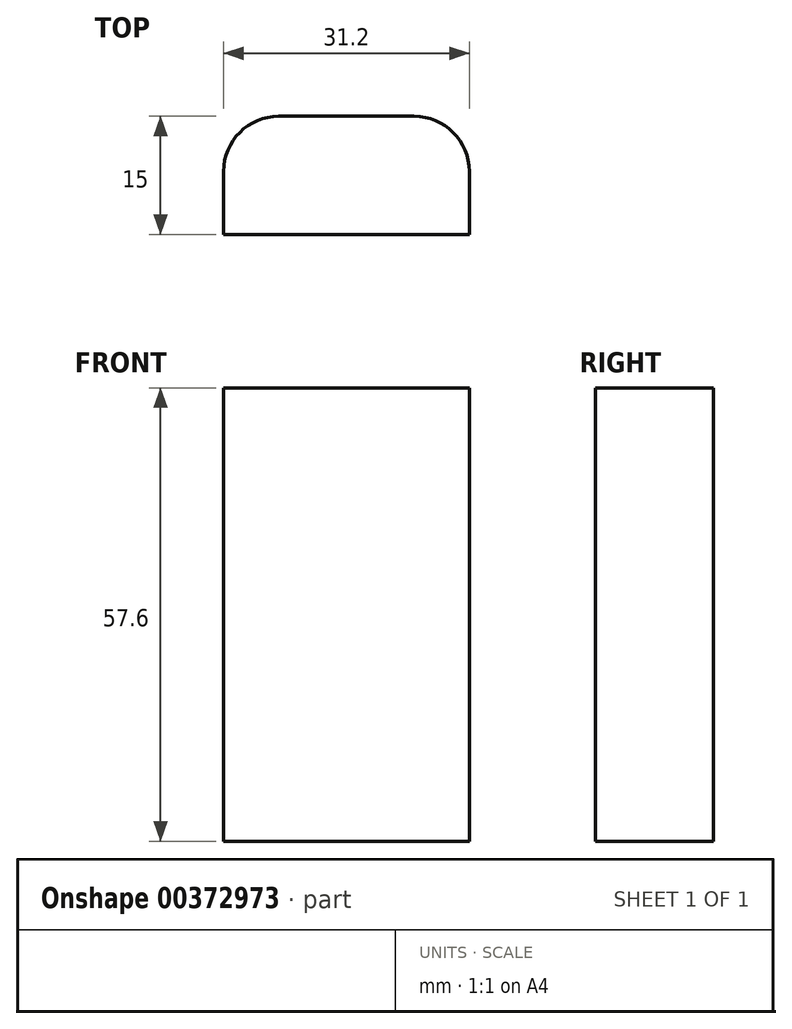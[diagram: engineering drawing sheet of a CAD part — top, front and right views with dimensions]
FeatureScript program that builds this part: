
annotation { "Feature Type Name" : "Feature", "Feature Type Description" : "" }
export const myFeature = defineFeature(function(context is Context, id is Id, definition is map)
    precondition{}
    {
        {
            var Q0;
            Q0=qCreatedBy(makeId("Top.planeOp"),FACE);
            var sketch = newSketch(context, id + "F0", { "sketchPlane" : qUnion([Q0])});
            skLineSegment(sketch, "E0.bottom", {"start": v(7, 15) * mm, "end": v(24.2, 15) * mm});
            skLineSegment(sketch, "E0.top", {"start": v(0, 0) * mm, "end": v(31.2, 0) * mm});
            skLineSegment(sketch, "E0.left", {"start": v(0, 8) * mm, "end": v(0, 0) * mm});
            skLineSegment(sketch, "E0.right", {"start": v(31.2, 8) * mm, "end": v(31.2, 0) * mm});
            skPoint(sketch, "E1.visualSharp", {"position": v(31.2, 15) * mm});
            skArc(sketch, "E1.filletArc", {"start": v(31.2, 8) * mm, "mid": v(29.15, 12.95) * mm, "end": v(24.2, 15) * mm});
            skPoint(sketch, "E2.visualSharp", {"position": v(0, 15) * mm});
            skArc(sketch, "E2.filletArc", {"start": v(7, 15) * mm, "mid": v(2.05, 12.95) * mm, "end": v(0, 8) * mm});
            skSolve(sketch);
        }
        {
            var Q0;
            Q0 = qSketchRegion(id + "F0", true);
            extrude(context, id + "F1", {"entities" : qUnion([Q0]), "depth" : 57.6 * mm, "offsetDistance" : 25 * mm, "symmetric" : true});
        }
    });
